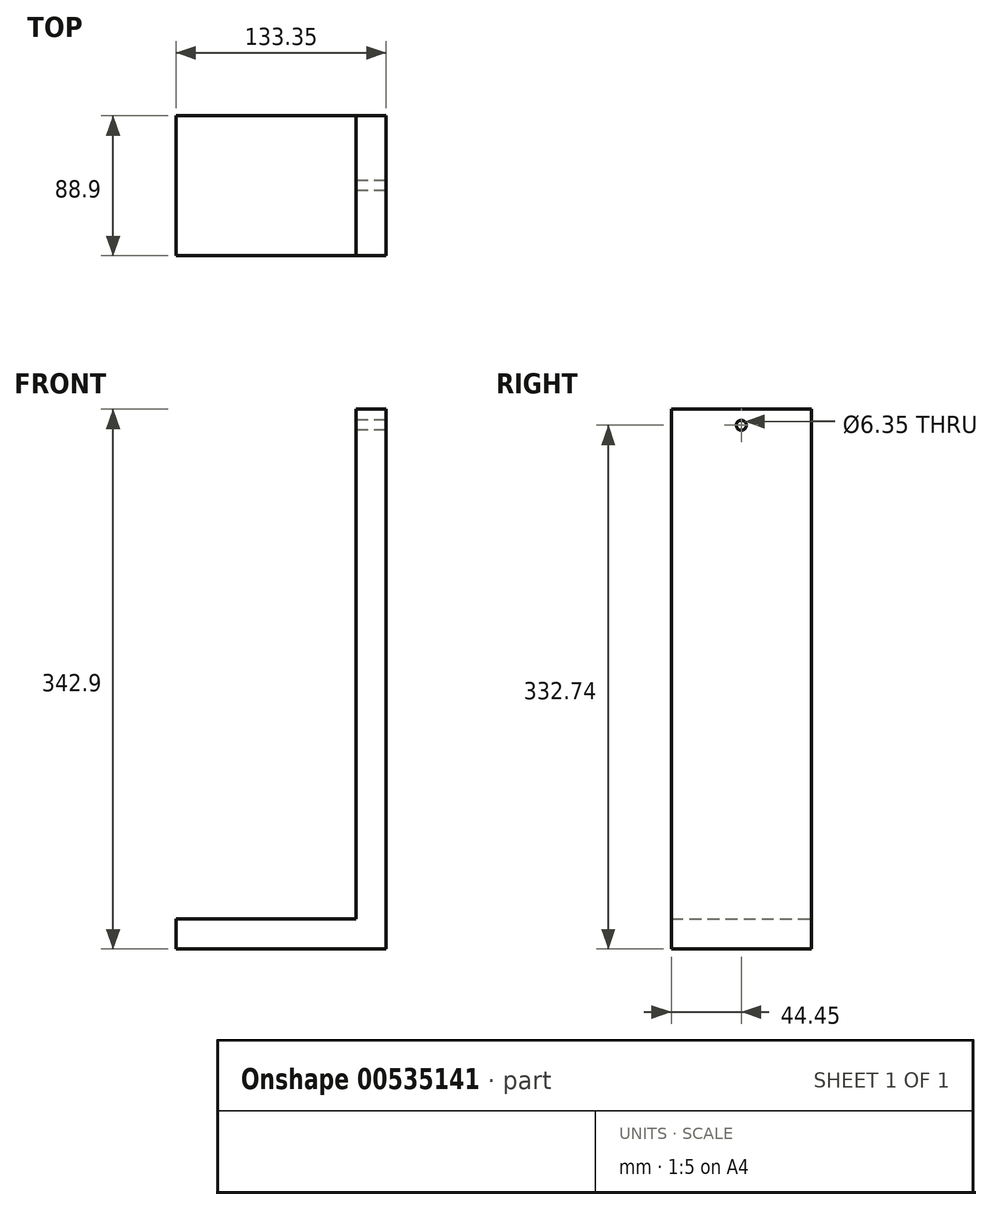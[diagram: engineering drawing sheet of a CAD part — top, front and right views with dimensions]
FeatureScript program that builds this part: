
annotation { "Feature Type Name" : "Feature", "Feature Type Description" : "" }
export const myFeature = defineFeature(function(context is Context, id is Id, definition is map)
    precondition{}
    {
        {
            var Q0;
            Q0=qCreatedBy(makeId("Front.planeOp"),FACE);
            var sketch = newSketch(context, id + "F0", { "sketchPlane" : qUnion([Q0])});
            skLineSegment(sketch, "E0", {"start": v(0, 0) * mm, "end": v(0, 342.9) * mm});
            skLineSegment(sketch, "E1", {"start": v(0, 342.9) * mm, "end": v(-19.05, 342.9) * mm});
            skLineSegment(sketch, "E2", {"start": v(-19.05, 342.9) * mm, "end": v(-19.05, 19.05) * mm});
            skLineSegment(sketch, "E3", {"start": v(-19.05, 19.05) * mm, "end": v(-133.35, 19.05) * mm});
            skLineSegment(sketch, "E4", {"start": v(-133.35, 19.05) * mm, "end": v(-133.35, 0) * mm});
            skLineSegment(sketch, "E5", {"start": v(-133.35, 0) * mm, "end": v(0, 0) * mm});
            skSolve(sketch);
        }
        {
            var Q0;
            Q0=makeQuery(id+"F0.imprint","IMPRINT",FACE,{"disambiguationData":[TD([[makeQuery(id+"F0.imprint","IMPRINT",EDGE,{"derivedFrom":sQuery(id+"F0.wireOp",EDGE,"E0")}),1.0]])]});
            extrude(context, id + "F1", {"entities" : qUnion([Q0]), "depth" : 88.9 * mm});
        }
        {
            var Q0;
            Q0=makeQuery(id+"F1.opExtrude","SWEPT_FACE",FACE,{"disambiguationData":[OSD([sQuery(id+"F0.wireOp",EDGE,"E2")])]});
            var sketch = newSketch(context, id + "F2", { "sketchPlane" : qUnion([Q0])});
            skLineSegment(sketch, "E6", {"start": v(0, 342.9) * mm, "end": v(44.45, 342.9) * mm});
            skLineSegment(sketch, "E7", {"start": v(44.45, 342.9) * mm, "end": v(44.45, 332.74) * mm});
            skSolve(sketch);
        }
        {
            var Q0;
            Q0=sQuery(id+"F2.wireOp",VERTEX,"E7.end");
            var Q1;
            Q1=makeQuery(id+"F1.opExtrude","SWEPT_BODY",BODY,{"disambiguationData":[OSD([sQuery(id+"F0.wireOp",EDGE,"E0"),sQuery(id+"F0.wireOp",EDGE,"E1"),sQuery(id+"F0.wireOp",EDGE,"E2"),sQuery(id+"F0.wireOp",EDGE,"E3"),sQuery(id+"F0.wireOp",EDGE,"E4"),sQuery(id+"F0.wireOp",EDGE,"E5")])]});
            hole(context, id + "F3", {"style" : HoleStyle.SIMPLE, "endStyle" : HoleEndStyle.THROUGH, "holeDiameter" : 6.35 * mm, "isTappedThrough" : true, "tappedDepth" : 12.7 * mm, "tapClearance" : 3, "locations" : qUnion([Q0]), "scope" : qUnion([Q1])});
        }
    });
